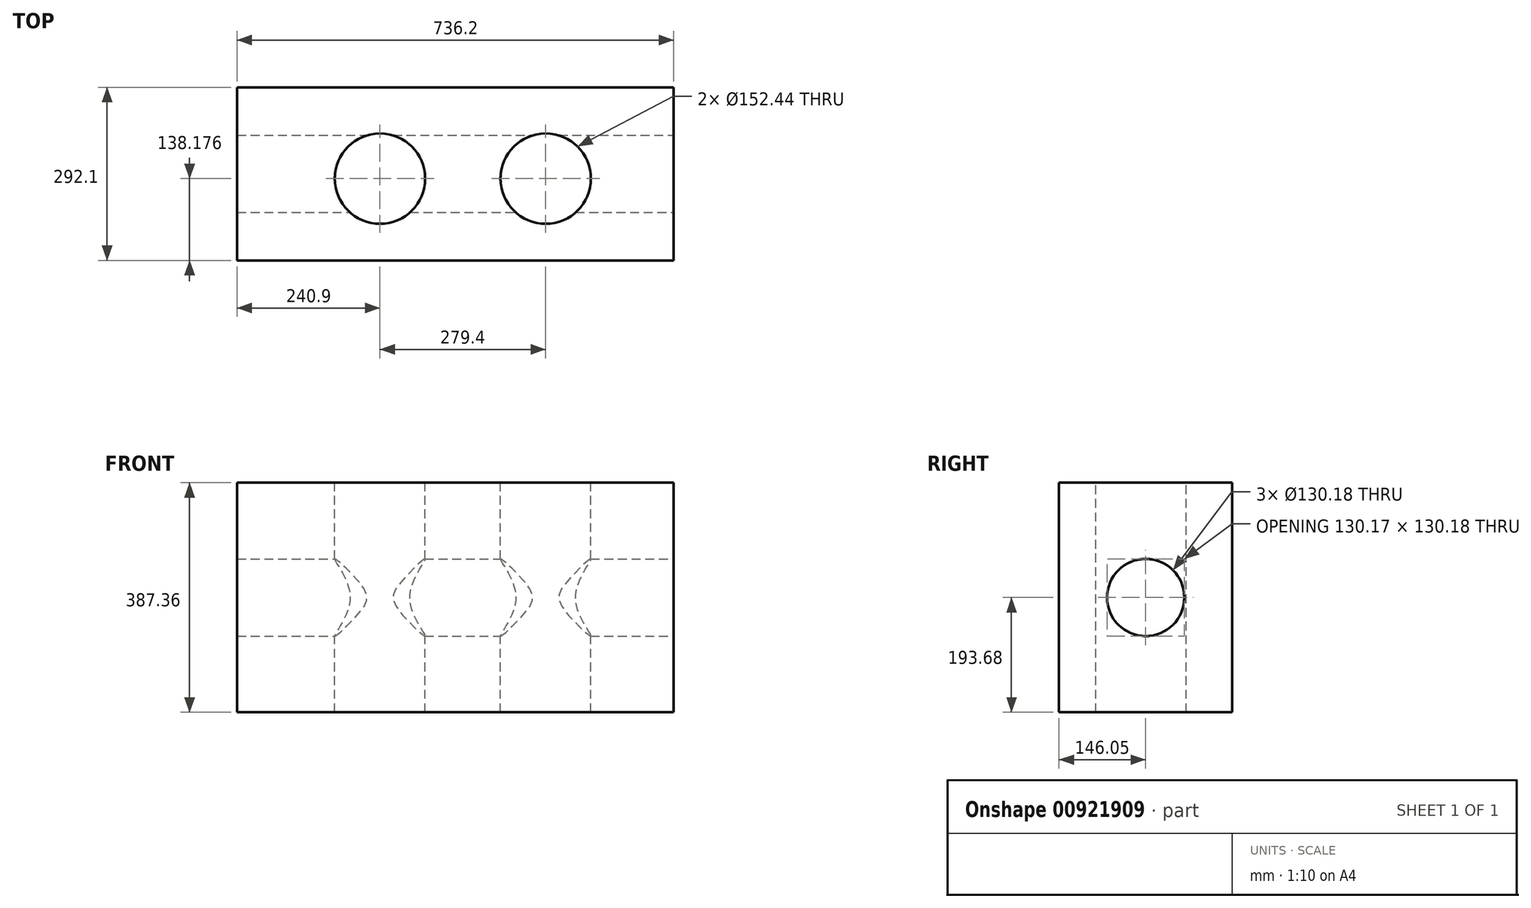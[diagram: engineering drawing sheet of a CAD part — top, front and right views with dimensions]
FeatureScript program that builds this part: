
annotation { "Feature Type Name" : "Feature", "Feature Type Description" : "" }
export const myFeature = defineFeature(function(context is Context, id is Id, definition is map)
    precondition{}
    {
        {
            var Q0;
            Q0=qCreatedBy(makeId("Front.planeOp"),FACE);
            var sketch = newSketch(context, id + "F0", { "sketchPlane" : qUnion([Q0])});
            skLineSegment(sketch, "E0.bottom", {"start": v(-355.6, 193.67) * mm, "end": v(355.6, 193.68) * mm});
            skLineSegment(sketch, "E0.top", {"start": v(-355.6, -193.68) * mm, "end": v(355.6, -193.67) * mm});
            skLineSegment(sketch, "E0.left", {"start": v(-355.6, 193.67) * mm, "end": v(-355.6, -193.68) * mm});
            skLineSegment(sketch, "E0.right", {"start": v(355.6, 193.68) * mm, "end": v(355.6, -193.67) * mm});
            skSolve(sketch);
        }
        {
            var Q0;
            Q0=makeQuery(id+"F0.imprint","IMPRINT",FACE,{"disambiguationData":[TD([[makeQuery(id+"F0.imprint","IMPRINT",EDGE,{"derivedFrom":sQuery(id+"F0.wireOp",EDGE,"E0.bottom")}),-1.0]])]});
            extrude(context, id + "F1", {"entities" : qUnion([Q0]), "oppositeDirection" : true, "depth" : 292.1 * mm, "offsetDistance" : 25 * mm});
        }
        {
            var Q0;
            Q0=qCreatedBy(makeId("Right.planeOp"),FACE);
            var sketch = newSketch(context, id + "F2", { "sketchPlane" : qUnion([Q0])});
            skCircle(sketch, "E1", {"center": v(146.05, 0) * mm, "radius": 65.09 * mm});
            skSolve(sketch);
        }
        {
            var Q0;
            Q0 = qSketchRegion(id + "F2", true);
            extrude(context, id + "F3", {"entities" : qUnion([Q0]), "operationType" : NewBodyOperationType.REMOVE, "endBound" : BoundingType.SYMMETRIC, "oppositeDirection" : true, "depth" : 750 * mm, "offsetDistance" : 25 * mm});
        }
        {
            var Q0;
            Q0=makeQuery(id+"F1.opExtrude","SWEPT_FACE",FACE,{"disambiguationData":[OSD([sQuery(id+"F0.wireOp",EDGE,"E0.bottom")])]});
            var sketch = newSketch(context, id + "F4", { "sketchPlane" : qUnion([Q0])});
            skCircle(sketch, "E2", {"center": v(139.7, 138.18) * mm, "radius": 76.22 * mm});
            skCircle(sketch, "E3", {"center": v(-139.7, 138.18) * mm, "radius": 76.22 * mm});
            skSolve(sketch);
        }
        {
            var Q0;
            Q0 = qSketchRegion(id + "F4", true);
            extrude(context, id + "F5", {"entities" : qUnion([Q0]), "operationType" : NewBodyOperationType.REMOVE, "oppositeDirection" : true, "depth" : 388 * mm, "offsetDistance" : 25 * mm});
        }
        {
            var Q0;
            Q0=qCreatedBy(makeId("Right.planeOp"),FACE);
            cPlane(context, id + "F6", {"entities" : qUnion([Q0]), "cplaneType" : CPlaneType.OFFSET, "offset" : 355.6 * mm, "oppositeDirection" : true, "width" : 150 * mm, "height" : 150 * mm});
        }
        {
            var Q0;
            Q0=makeQuery(id+"F1.opExtrude","SWEPT_FACE",FACE,{"disambiguationData":[OSD([sQuery(id+"F0.wireOp",EDGE,"E0.left")])]});
            extrude(context, id + "F7", {"entities" : qUnion([Q0]), "operationType" : NewBodyOperationType.ADD, "depth" : 25 * mm, "offsetDistance" : 25 * mm});
        }
    });
